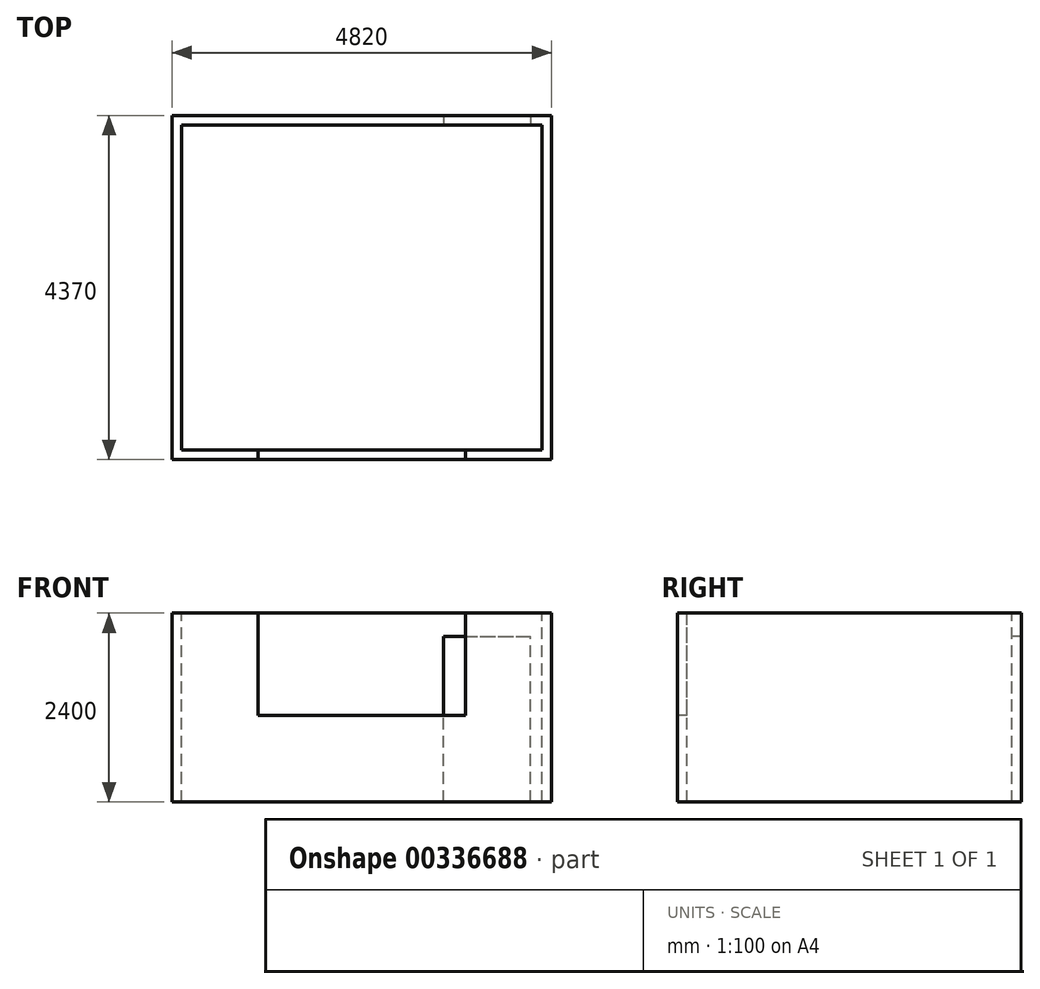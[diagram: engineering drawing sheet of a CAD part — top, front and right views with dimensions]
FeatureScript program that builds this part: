
annotation { "Feature Type Name" : "Feature", "Feature Type Description" : "" }
export const myFeature = defineFeature(function(context is Context, id is Id, definition is map)
    precondition{}
    {
        {
            var Q0;
            Q0=qCreatedBy(makeId("Top.planeOp"),FACE);
            var sketch = newSketch(context, id + "F0", { "sketchPlane" : qUnion([Q0])});
            skLineSegment(sketch, "E0.bottom", {"start": v(-2500, -2185) * mm, "end": v(2320, -2185) * mm});
            skLineSegment(sketch, "E0.top", {"start": v(-2500, 2185) * mm, "end": v(2320, 2185) * mm});
            skLineSegment(sketch, "E0.left", {"start": v(-2500, -2185) * mm, "end": v(-2500, 2185) * mm});
            skLineSegment(sketch, "E0.right", {"start": v(2320, -2185) * mm, "end": v(2320, 2185) * mm});
            skSolve(sketch);
        }
        {
            var Q0;
            Q0 = qSketchRegion(id + "F0", true);
            extrude(context, id + "F1", {"entities" : qUnion([Q0]), "depth" : 2400 * mm});
        }
        {
            var Q0;
            Q0=makeQuery(id+"F1.opExtrude","CAP_FACE",FACE,{"disambiguationData":[OSD([sQuery(id+"F0.wireOp",EDGE,"E0.bottom"),sQuery(id+"F0.wireOp",EDGE,"E0.top"),sQuery(id+"F0.wireOp",EDGE,"E0.left"),sQuery(id+"F0.wireOp",EDGE,"E0.right")])],"isStart":false});
            var sketch = newSketch(context, id + "F2", { "sketchPlane" : qUnion([Q0])});
            skLineSegment(sketch, "E1.bottom", {"start": v(-2380, -2065) * mm, "end": v(2200, -2065) * mm});
            skLineSegment(sketch, "E1.top", {"start": v(-2380, 2065) * mm, "end": v(2200, 2065) * mm});
            skLineSegment(sketch, "E1.left", {"start": v(-2380, -2065) * mm, "end": v(-2380, 2065) * mm});
            skLineSegment(sketch, "E1.right", {"start": v(2200, -2065) * mm, "end": v(2200, 2065) * mm});
            skSolve(sketch);
        }
        {
            var Q0;
            Q0 = qSketchRegion(id + "F2", true);
            extrude(context, id + "F3", {"entities" : qUnion([Q0]), "operationType" : NewBodyOperationType.REMOVE, "endBound" : BoundingType.UP_TO_NEXT, "oppositeDirection" : true, "depth" : 25 * mm});
        }
        {
            var Q0;
            Q0=makeQuery(id+"F1.opExtrude","SWEPT_FACE",FACE,{"disambiguationData":[OSD([sQuery(id+"F0.wireOp",EDGE,"E0.bottom")])]});
            var sketch = newSketch(context, id + "F4", { "sketchPlane" : qUnion([Q0])});
            skLineSegment(sketch, "E2.bottom", {"start": v(-1410, 2400) * mm, "end": v(1230, 2400) * mm});
            skLineSegment(sketch, "E2.top", {"start": v(-1410, 1100) * mm, "end": v(1230, 1100) * mm});
            skLineSegment(sketch, "E2.left", {"start": v(-1410, 2400) * mm, "end": v(-1410, 1100) * mm});
            skLineSegment(sketch, "E2.right", {"start": v(1230, 2400) * mm, "end": v(1230, 1100) * mm});
            skSolve(sketch);
        }
        {
            var Q0;
            Q0 = qSketchRegion(id + "F4", true);
            extrude(context, id + "F5", {"entities" : qUnion([Q0]), "operationType" : NewBodyOperationType.REMOVE, "endBound" : BoundingType.UP_TO_NEXT, "oppositeDirection" : true, "depth" : 25 * mm});
        }
        {
            var Q0;
            Q0=makeQuery(id+"F3.boolean.opBoolean","COPY",FACE,{"derivedFrom":makeQuery(id+"F3.opExtrude","SWEPT_FACE",FACE,{"disambiguationData":[OSD([sQuery(id+"F2.wireOp",EDGE,"E1.top")])]})});
            var sketch = newSketch(context, id + "F6", { "sketchPlane" : qUnion([Q0])});
            skLineSegment(sketch, "E3.bottom", {"start": v(950, 0) * mm, "end": v(2050, 0) * mm});
            skLineSegment(sketch, "E3.top", {"start": v(950, 2100) * mm, "end": v(2050, 2100) * mm});
            skLineSegment(sketch, "E3.left", {"start": v(950, 0) * mm, "end": v(950, 2100) * mm});
            skLineSegment(sketch, "E3.right", {"start": v(2050, 0) * mm, "end": v(2050, 2100) * mm});
            skSolve(sketch);
        }
        {
            var Q0;
            Q0 = qSketchRegion(id + "F6", true);
            extrude(context, id + "F7", {"entities" : qUnion([Q0]), "operationType" : NewBodyOperationType.REMOVE, "endBound" : BoundingType.UP_TO_NEXT, "oppositeDirection" : true, "depth" : 25 * mm});
        }
    });
